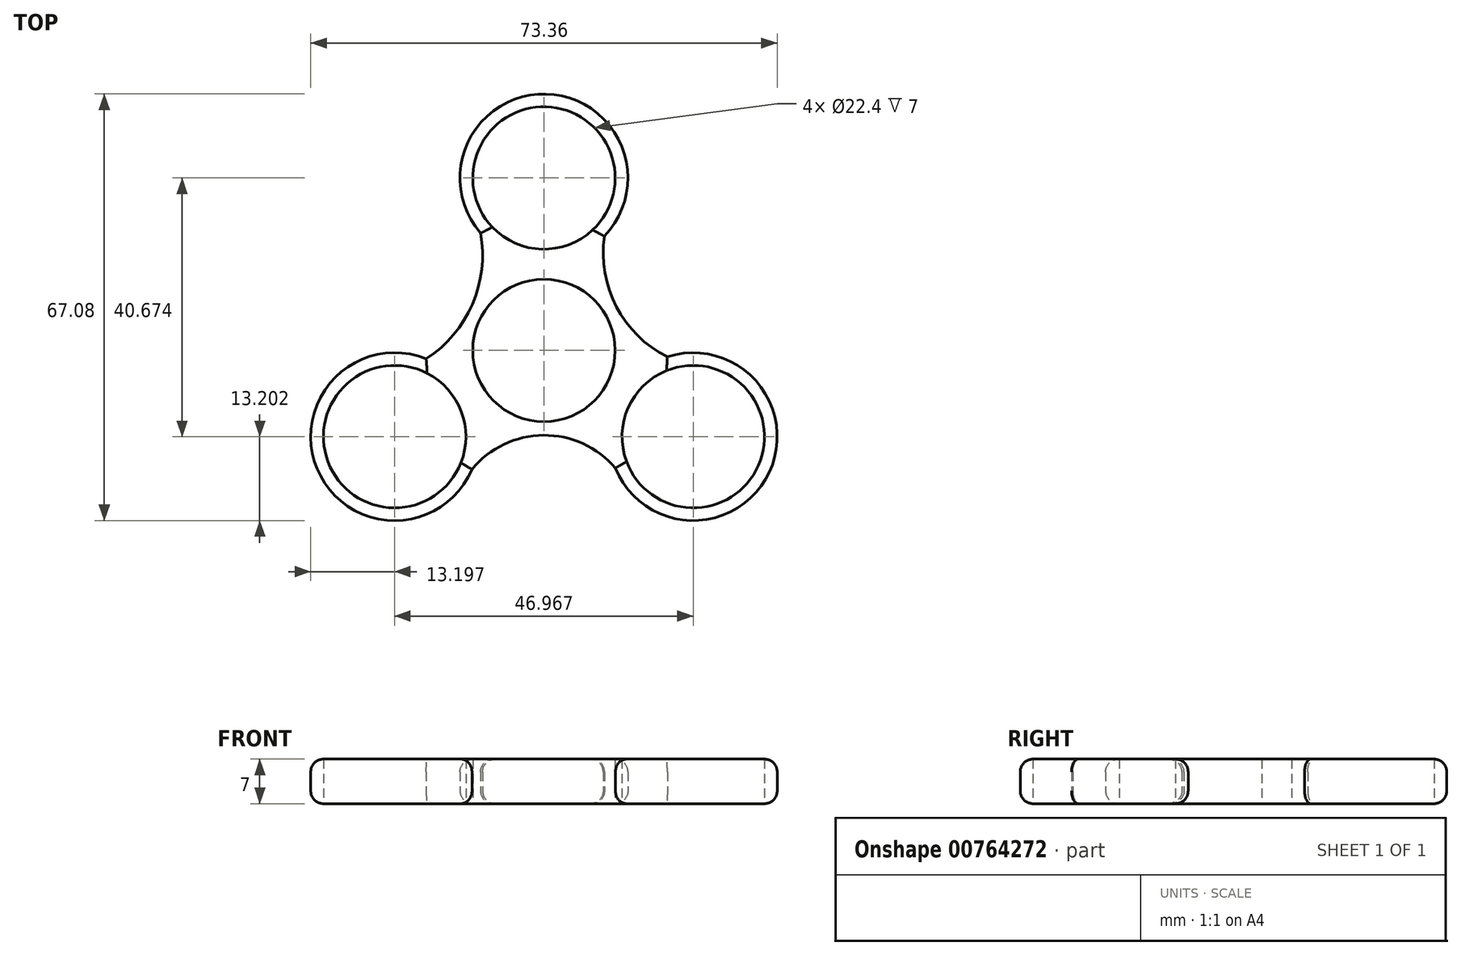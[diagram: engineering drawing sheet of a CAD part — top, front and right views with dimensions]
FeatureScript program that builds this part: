
annotation { "Feature Type Name" : "Feature", "Feature Type Description" : "" }
export const myFeature = defineFeature(function(context is Context, id is Id, definition is map)
    precondition{}
    {
        {
            var Q0;
            Q0=qCreatedBy(makeId("Top.planeOp"),FACE);
            var sketch = newSketch(context, id + "F0", { "sketchPlane" : qUnion([Q0])});
            skCircle(sketch, "E0", {"center": v(0, 0) * mm, "radius": 11.2 * mm});
            skCircle(sketch, "E1", {"center": v(0, 27.12) * mm, "radius": 11.2 * mm});
            skCircle(sketch, "E2", {"center": v(0, 27.12) * mm, "radius": 13.2 * mm});
            skCircle(sketch, "E3.1.0", {"center": v(-23.48, -13.56) * mm, "radius": 11.2 * mm});
            skCircle(sketch, "E3.2.0", {"center": v(23.48, -13.56) * mm, "radius": 11.2 * mm});
            skCircle(sketch, "E4.1.0", {"center": v(-23.48, -13.56) * mm, "radius": 13.2 * mm});
            skCircle(sketch, "E4.2.0", {"center": v(23.48, -13.56) * mm, "radius": 13.2 * mm});
            skArc(sketch, "E5", {"start": v(9.52, 17.97) * mm, "mid": v(11.39, 6.88) * mm, "end": v(19.41, -1) * mm});
            skArc(sketch, "E6", {"start": v(-18.52, -1.33) * mm, "mid": v(-11.26, 7.28) * mm, "end": v(-9.96, 18.46) * mm});
            skArc(sketch, "E7", {"start": v(11.25, -18.5) * mm, "mid": v(-0.08, -13.33) * mm, "end": v(-11.33, -18.7) * mm});
            skSolve(sketch);
        }
        {
            var Q0;
            Q0=makeQuery(id+"F0.imprint","IMPRINT",FACE,{"disambiguationData":[TD([[makeQuery(id+"F0.imprint","IMPRINT",EDGE,{"derivedFrom":sQuery(id+"F0.wireOp",EDGE,"E1")}),-1.0]])]});
            var Q1;
            Q1=makeQuery(id+"F0.imprint","IMPRINT",FACE,{"disambiguationData":[TD([[makeQuery(id+"F0.imprint","IMPRINT",EDGE,{"derivedFrom":sQuery(id+"F0.wireOp",EDGE,"E0")}),-1.0]])]});
            var Q2;
            Q2=makeQuery(id+"F0.imprint","IMPRINT",FACE,{"disambiguationData":[TD([[makeQuery(id+"F0.imprint","IMPRINT",EDGE,{"derivedFrom":sQuery(id+"F0.wireOp",EDGE,"E3.1.0")}),-1.0]])]});
            var Q3;
            Q3=makeQuery(id+"F0.imprint","IMPRINT",FACE,{"disambiguationData":[TD([[makeQuery(id+"F0.imprint","IMPRINT",EDGE,{"derivedFrom":sQuery(id+"F0.wireOp",EDGE,"E3.2.0")}),-1.0]])]});
            extrude(context, id + "F1", {"entities" : qUnion([Q0, Q1, Q2, Q3]), "depth" : 7 * mm, "offsetDistance" : 25 * mm});
        }
        {
            var Q0;
            Q0=makeQuery(id+"F1.opExtrude","CAP_EDGE",EDGE,{"disambiguationData":[OSD([sQuery(id+"F0.wireOp",EDGE,"E4.1.0")])],"isStart":false});
            var Q1;
            Q1=makeQuery(id+"F1.opExtrude","CAP_EDGE",EDGE,{"disambiguationData":[OSD([sQuery(id+"F0.wireOp",EDGE,"E6")])],"isStart":false});
            var Q2;
            Q2=makeQuery(id+"F1.opExtrude","CAP_EDGE",EDGE,{"disambiguationData":[OSD([sQuery(id+"F0.wireOp",EDGE,"E2")])],"isStart":false});
            var Q3;
            Q3=makeQuery(id+"F1.opExtrude","CAP_EDGE",EDGE,{"disambiguationData":[OSD([sQuery(id+"F0.wireOp",EDGE,"E5")])],"isStart":false});
            var Q4;
            Q4=makeQuery(id+"F1.opExtrude","CAP_EDGE",EDGE,{"disambiguationData":[OSD([sQuery(id+"F0.wireOp",EDGE,"E4.2.0")])],"isStart":false});
            var Q5;
            Q5=makeQuery(id+"F1.opExtrude","CAP_EDGE",EDGE,{"disambiguationData":[OSD([sQuery(id+"F0.wireOp",EDGE,"E7")])],"isStart":false});
            fillet(context, id + "F2", {"entities" : qUnion([Q0, Q1, Q2, Q3, Q4, Q5]), "radius" : 2 * mm, "tangentPropagation" : true, "allowEdgeOverflow" : false});
        }
        {
            var Q0;
            Q0=makeQuery(id+"F1.opExtrude","CAP_EDGE",EDGE,{"disambiguationData":[OSD([sQuery(id+"F0.wireOp",EDGE,"E4.1.0")])],"isStart":true});
            var Q1;
            Q1=makeQuery(id+"F1.opExtrude","CAP_EDGE",EDGE,{"disambiguationData":[OSD([sQuery(id+"F0.wireOp",EDGE,"E7")])],"isStart":true});
            var Q2;
            Q2=makeQuery(id+"F1.opExtrude","CAP_EDGE",EDGE,{"disambiguationData":[OSD([sQuery(id+"F0.wireOp",EDGE,"E6")])],"isStart":true});
            var Q3;
            Q3=makeQuery(id+"F1.opExtrude","CAP_EDGE",EDGE,{"disambiguationData":[OSD([sQuery(id+"F0.wireOp",EDGE,"E2")])],"isStart":true});
            var Q4;
            Q4=makeQuery(id+"F1.opExtrude","CAP_EDGE",EDGE,{"disambiguationData":[OSD([sQuery(id+"F0.wireOp",EDGE,"E5")])],"isStart":true});
            var Q5;
            Q5=makeQuery(id+"F1.opExtrude","CAP_EDGE",EDGE,{"disambiguationData":[OSD([sQuery(id+"F0.wireOp",EDGE,"E4.2.0")])],"isStart":true});
            fillet(context, id + "F3", {"entities" : qUnion([Q0, Q1, Q2, Q3, Q4, Q5]), "radius" : 2 * mm, "tangentPropagation" : true, "allowEdgeOverflow" : false});
        }
    });
